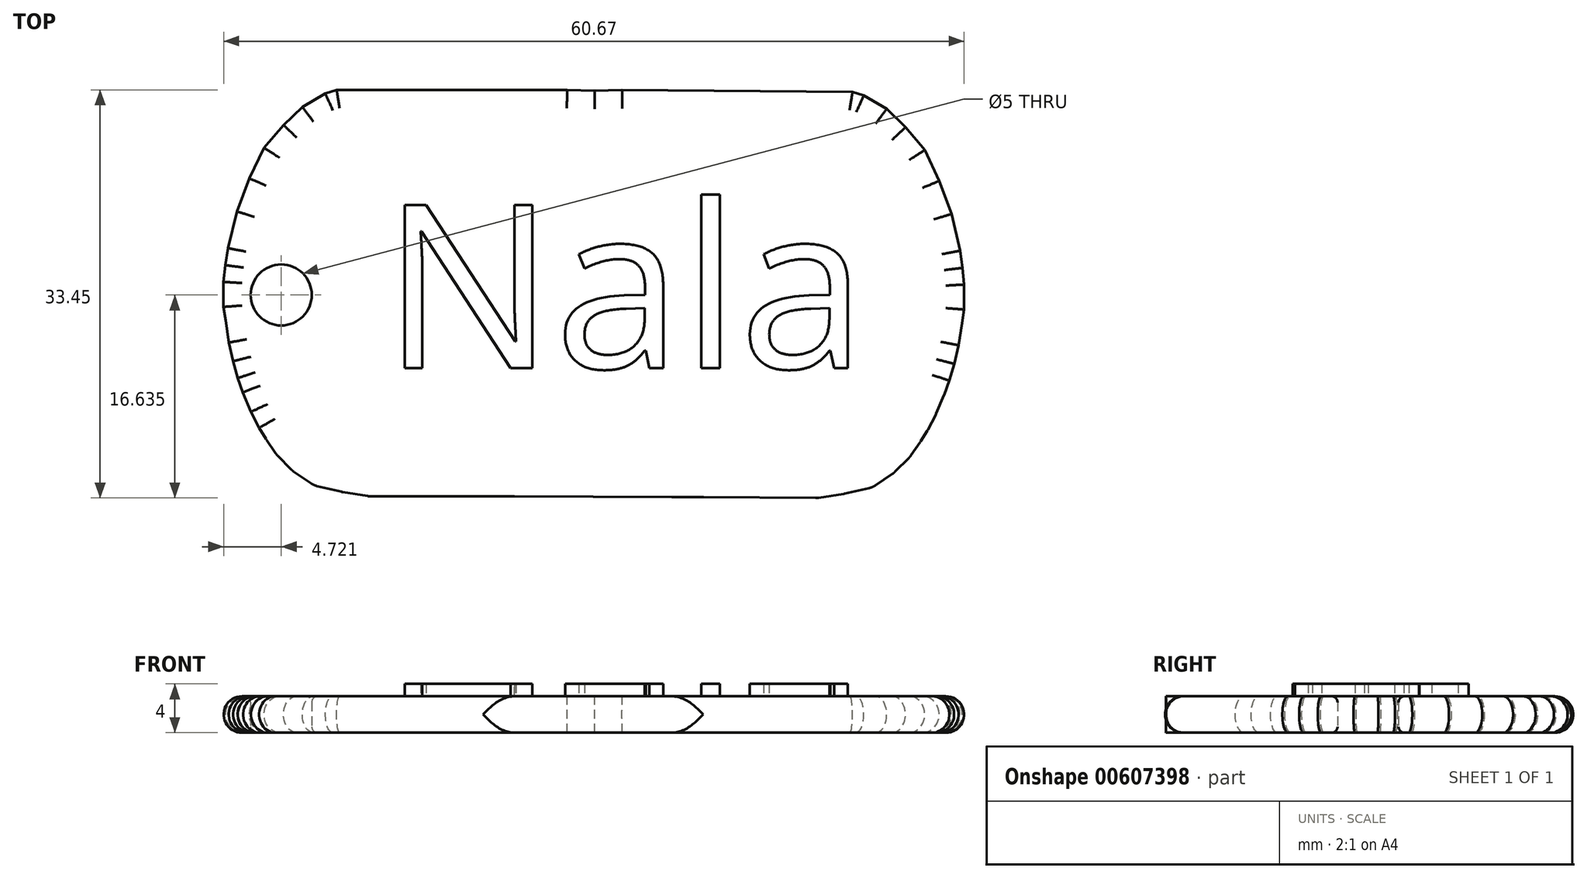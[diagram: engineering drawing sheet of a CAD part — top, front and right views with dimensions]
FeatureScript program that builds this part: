
annotation { "Feature Type Name" : "Feature", "Feature Type Description" : "" }
export const myFeature = defineFeature(function(context is Context, id is Id, definition is map)
    precondition{}
    {
        {
            var Q0;
            Q0=qCreatedBy(makeId("Top.planeOp"),FACE);
            var sketch = newSketch(context, id + "F0", { "sketchPlane" : qUnion([Q0])});
            skLineSegment(sketch, "E0", {"start": v(-37.9, 10.65) * mm, "end": v(-39.11, 8.12) * mm});
            skLineSegment(sketch, "E1", {"start": v(-39.11, 8.12) * mm, "end": v(-40.13, 5.41) * mm});
            skLineSegment(sketch, "E2", {"start": v(-40.13, 5.41) * mm, "end": v(-40.85, 2.4) * mm});
            skLineSegment(sketch, "E3", {"start": v(-40.85, 2.4) * mm, "end": v(-41.06, 1) * mm});
            skLineSegment(sketch, "E4", {"start": v(-41.06, 1) * mm, "end": v(-41.21, -0.37) * mm});
            skLineSegment(sketch, "E5", {"start": v(-41.21, -0.37) * mm, "end": v(-41.21, -2.41) * mm});
            skLineSegment(sketch, "E6", {"start": v(-41.21, -2.41) * mm, "end": v(-41.05, -3.53) * mm});
            skLineSegment(sketch, "E7", {"start": v(-41.05, -3.53) * mm, "end": v(-40.8, -5.34) * mm});
            skLineSegment(sketch, "E8", {"start": v(-40.8, -5.34) * mm, "end": v(-40.44, -6.87) * mm});
            skLineSegment(sketch, "E9", {"start": v(-40.44, -6.87) * mm, "end": v(-40.07, -8.25) * mm});
            skLineSegment(sketch, "E10", {"start": v(-40.07, -8.25) * mm, "end": v(-39.63, -9.42) * mm});
            skLineSegment(sketch, "E11", {"start": v(-39.63, -9.42) * mm, "end": v(-38.98, -11.01) * mm});
            skLineSegment(sketch, "E12", {"start": v(-38.98, -11.01) * mm, "end": v(-38.3, -12.33) * mm});
            skLineSegment(sketch, "E13", {"start": v(-38.3, -12.33) * mm, "end": v(-37.72, -13.27) * mm});
            skLineSegment(sketch, "E14", {"start": v(-37.72, -13.27) * mm, "end": v(-36.88, -14.5) * mm});
            skLineSegment(sketch, "E15", {"start": v(-36.88, -14.5) * mm, "end": v(-35.56, -15.85) * mm});
            skLineSegment(sketch, "E16", {"start": v(-35.56, -15.85) * mm, "end": v(-33.8, -17.04) * mm});
            skLineSegment(sketch, "E17", {"start": v(-33.8, -17.04) * mm, "end": v(-31.5, -17.58) * mm});
            skLineSegment(sketch, "E18", {"start": v(-31.5, -17.58) * mm, "end": v(-29.29, -17.94) * mm});
            skLineSegment(sketch, "E19", {"start": v(-29.29, -17.94) * mm, "end": v(-19.97, -17.94) * mm});
            skLineSegment(sketch, "E20", {"start": v(-37.9, 10.65) * mm, "end": v(-36.3, 12.49) * mm});
            skLineSegment(sketch, "E21", {"start": v(-36.3, 12.49) * mm, "end": v(-34.77, 13.98) * mm});
            skLineSegment(sketch, "E22", {"start": v(-34.77, 13.98) * mm, "end": v(-32.87, 15.08) * mm});
            skLineSegment(sketch, "E23", {"start": v(-32.87, 15.08) * mm, "end": v(-31.95, 15.38) * mm});
            skLineSegment(sketch, "E24", {"start": v(-31.95, 15.38) * mm, "end": v(-30.53, 15.38) * mm});
            skLineSegment(sketch, "E25", {"start": v(-30.53, 15.38) * mm, "end": v(-28.67, 15.38) * mm});
            skLineSegment(sketch, "E26", {"start": v(-28.67, 15.38) * mm, "end": v(-26.55, 15.38) * mm});
            skLineSegment(sketch, "E27", {"start": v(-26.55, 15.38) * mm, "end": v(-23.52, 15.38) * mm});
            skLineSegment(sketch, "E28", {"start": v(-23.52, 15.38) * mm, "end": v(-18.18, 15.38) * mm});
            skLineSegment(sketch, "E29", {"start": v(-18.18, 15.38) * mm, "end": v(-13.07, 15.38) * mm});
            skLineSegment(sketch, "E30", {"start": v(-13.07, 15.38) * mm, "end": v(-10.82, 15.3) * mm});
            skLineSegment(sketch, "E31", {"start": v(-10.82, 15.3) * mm, "end": v(-10.94, -17.58) * mm});
            skLineSegment(sketch, "E32.MirrorCS", {"start": v(-8.57, 15.36) * mm, "end": v(-10.82, 15.3) * mm});
            skLineSegment(sketch, "E33.MirrorCS", {"start": v(-3.46, 15.32) * mm, "end": v(-8.57, 15.36) * mm});
            skLineSegment(sketch, "E34.MirrorCS", {"start": v(1.88, 15.28) * mm, "end": v(-3.46, 15.32) * mm});
            skLineSegment(sketch, "E35.MirrorCS", {"start": v(4.91, 15.26) * mm, "end": v(1.88, 15.28) * mm});
            skLineSegment(sketch, "E36.MirrorCS", {"start": v(7.03, 15.25) * mm, "end": v(4.91, 15.26) * mm});
            skLineSegment(sketch, "E37.MirrorCS", {"start": v(8.9, 15.23) * mm, "end": v(7.03, 15.25) * mm});
            skLineSegment(sketch, "E38.MirrorCS", {"start": v(10.31, 15.22) * mm, "end": v(8.9, 15.23) * mm});
            skLineSegment(sketch, "E39.MirrorCS", {"start": v(11.23, 14.92) * mm, "end": v(10.31, 15.22) * mm});
            skLineSegment(sketch, "E40.MirrorCS", {"start": v(13.12, 13.8) * mm, "end": v(11.23, 14.92) * mm});
            skLineSegment(sketch, "E41.MirrorCS", {"start": v(14.65, 12.3) * mm, "end": v(13.12, 13.8) * mm});
            skLineSegment(sketch, "E42.MirrorCS", {"start": v(16.23, 10.45) * mm, "end": v(14.65, 12.3) * mm});
            skLineSegment(sketch, "E43.MirrorCS", {"start": v(16.23, 10.45) * mm, "end": v(17.42, 7.91) * mm});
            skLineSegment(sketch, "E44.MirrorCS", {"start": v(17.42, 7.91) * mm, "end": v(18.42, 5.2) * mm});
            skLineSegment(sketch, "E45.MirrorCS", {"start": v(18.42, 5.2) * mm, "end": v(19.12, 2.19) * mm});
            skLineSegment(sketch, "E46.MirrorCS", {"start": v(19.12, 2.19) * mm, "end": v(19.31, 0.79) * mm});
            skLineSegment(sketch, "E47.MirrorCS", {"start": v(19.31, 0.79) * mm, "end": v(19.46, -0.59) * mm});
            skLineSegment(sketch, "E48.MirrorCS", {"start": v(19.46, -0.59) * mm, "end": v(19.45, -2.63) * mm});
            skLineSegment(sketch, "E49.MirrorCS", {"start": v(19.45, -2.63) * mm, "end": v(19.27, -3.74) * mm});
            skLineSegment(sketch, "E50.MirrorCS", {"start": v(19.27, -3.74) * mm, "end": v(19, -5.55) * mm});
            skLineSegment(sketch, "E51.MirrorCS", {"start": v(19, -5.55) * mm, "end": v(18.64, -7.08) * mm});
            skLineSegment(sketch, "E52.MirrorCS", {"start": v(18.64, -7.08) * mm, "end": v(18.25, -8.46) * mm});
            skLineSegment(sketch, "E53.MirrorCS", {"start": v(18.25, -8.46) * mm, "end": v(17.8, -9.63) * mm});
            skLineSegment(sketch, "E54.MirrorCS", {"start": v(17.8, -9.63) * mm, "end": v(17.15, -11.21) * mm});
            skLineSegment(sketch, "E55.MirrorCS", {"start": v(17.15, -11.21) * mm, "end": v(16.47, -12.53) * mm});
            skLineSegment(sketch, "E56.MirrorCS", {"start": v(16.47, -12.53) * mm, "end": v(15.87, -13.46) * mm});
            skLineSegment(sketch, "E57.MirrorCS", {"start": v(15.87, -13.46) * mm, "end": v(15.03, -14.7) * mm});
            skLineSegment(sketch, "E58.MirrorCS", {"start": v(15.03, -14.7) * mm, "end": v(13.7, -16.02) * mm});
            skLineSegment(sketch, "E59.MirrorCS", {"start": v(13.7, -16.02) * mm, "end": v(11.93, -17.2) * mm});
            skLineSegment(sketch, "E60.MirrorCS", {"start": v(11.93, -17.2) * mm, "end": v(9.63, -17.73) * mm});
            skLineSegment(sketch, "E61.MirrorCS", {"start": v(9.63, -17.73) * mm, "end": v(7.4, -18.07) * mm});
            skLineSegment(sketch, "E62.MirrorCS", {"start": v(7.4, -18.07) * mm, "end": v(-1.9, -18) * mm});
            skCircle(sketch, "E63", {"center": v(-36.49, -1.43) * mm, "radius": 2.5 * mm});
            skLineSegment(sketch, "E64", {"start": v(-19.97, -17.94) * mm, "end": v(-1.9, -18) * mm});
            skSolve(sketch);
        }
        {
            var Q0;
            Q0 = qSketchRegion(id + "F0", true);
            var Q1;
            Q1=makeQuery(id+"F0.imprint","IMPRINT",FACE,{"disambiguationData":[TD([[makeQuery(id+"F0.imprint","IMPRINT",EDGE,{"derivedFrom":sQuery(id+"F0.wireOp",EDGE,"E0")}),1.0]])]});
            extrude(context, id + "F1", {"entities" : qUnion([Q0, Q1]), "depth" : 3 * mm, "offsetDistance" : 25 * mm});
        }
        {
            var Q0;
            Q0=makeQuery(id+"F1.opExtrude","CAP_EDGE",EDGE,{"disambiguationData":[OSD([sQuery(id+"F0.wireOp",EDGE,"E19")])],"isStart":false});
            var Q1;
            Q1=makeQuery(id+"F1.opExtrude","CAP_EDGE",EDGE,{"disambiguationData":[OSD([sQuery(id+"F0.wireOp",EDGE,"WqU1F3oS-ofhP-bZeb-JVwl-enVTnePdHite")])],"isStart":false});
            var Q2;
            Q2=makeQuery(id+"F1.opExtrude","CAP_EDGE",EDGE,{"disambiguationData":[OSD([sQuery(id+"F0.wireOp",EDGE,"QgttkmmI-ZrSr-rnyg-uRgk-pYvE0oLxrQIC"),sQuery(id+"F0.wireOp",EDGE,"cICnWOkE-zCsr-WVfL-8WAR-oVfGwmKeuLjA")])],"isStart":false});
            var Q3;
            Q3=makeQuery(id+"F1.opExtrude","CAP_EDGE",EDGE,{"disambiguationData":[OSD([sQuery(id+"F0.wireOp",EDGE,"5ab367f4-9cd3-4356-90f0-5b2019c22e200.MirrorCS"),sQuery(id+"F0.wireOp",EDGE,"096961d2-05df-4f17-8771-bd5e1e9e85af0.MirrorCS")])],"isStart":false});
            var Q4;
            Q4=makeQuery(id+"F1.opExtrude","CAP_EDGE",EDGE,{"disambiguationData":[OSD([sQuery(id+"F0.wireOp",EDGE,"e1c94456-ab08-4bec-9781-fa68d74f9dfd0.MirrorCS")])],"isStart":false});
            var Q5;
            Q5=makeQuery(id+"F1.opExtrude","CAP_EDGE",EDGE,{"disambiguationData":[OSD([sQuery(id+"F0.wireOp",EDGE,"E62.MirrorCS")])],"isStart":false});
            var Q6;
            Q6=makeQuery(id+"F1.opExtrude","CAP_EDGE",EDGE,{"disambiguationData":[OSD([sQuery(id+"F0.wireOp",EDGE,"E60.MirrorCS")])],"isStart":false});
            var Q7;
            Q7=makeQuery(id+"F1.opExtrude","CAP_EDGE",EDGE,{"disambiguationData":[OSD([sQuery(id+"F0.wireOp",EDGE,"E61.MirrorCS")])],"isStart":false});
            var Q8;
            Q8=makeQuery(id+"F1.opExtrude","CAP_EDGE",EDGE,{"disambiguationData":[OSD([sQuery(id+"F0.wireOp",EDGE,"E59.MirrorCS")])],"isStart":false});
            var Q9;
            Q9=makeQuery(id+"F1.opExtrude","CAP_EDGE",EDGE,{"disambiguationData":[OSD([sQuery(id+"F0.wireOp",EDGE,"E58.MirrorCS")])],"isStart":false});
            var Q10;
            Q10=makeQuery(id+"F1.opExtrude","CAP_EDGE",EDGE,{"disambiguationData":[OSD([sQuery(id+"F0.wireOp",EDGE,"E56.MirrorCS")])],"isStart":false});
            var Q11;
            Q11=makeQuery(id+"F1.opExtrude","CAP_EDGE",EDGE,{"disambiguationData":[OSD([sQuery(id+"F0.wireOp",EDGE,"E57.MirrorCS")])],"isStart":false});
            var Q12;
            Q12=makeQuery(id+"F1.opExtrude","CAP_EDGE",EDGE,{"disambiguationData":[OSD([sQuery(id+"F0.wireOp",EDGE,"E55.MirrorCS")])],"isStart":false});
            var Q13;
            Q13=makeQuery(id+"F1.opExtrude","CAP_EDGE",EDGE,{"disambiguationData":[OSD([sQuery(id+"F0.wireOp",EDGE,"E54.MirrorCS")])],"isStart":false});
            var Q14;
            Q14=makeQuery(id+"F1.opExtrude","CAP_EDGE",EDGE,{"disambiguationData":[OSD([sQuery(id+"F0.wireOp",EDGE,"E53.MirrorCS")])],"isStart":false});
            var Q15;
            Q15=makeQuery(id+"F1.opExtrude","CAP_EDGE",EDGE,{"disambiguationData":[OSD([sQuery(id+"F0.wireOp",EDGE,"E52.MirrorCS")])],"isStart":false});
            var Q16;
            Q16=makeQuery(id+"F1.opExtrude","CAP_EDGE",EDGE,{"disambiguationData":[OSD([sQuery(id+"F0.wireOp",EDGE,"E51.MirrorCS")])],"isStart":false});
            var Q17;
            Q17=makeQuery(id+"F1.opExtrude","CAP_EDGE",EDGE,{"disambiguationData":[OSD([sQuery(id+"F0.wireOp",EDGE,"E50.MirrorCS")])],"isStart":false});
            var Q18;
            Q18=makeQuery(id+"F1.opExtrude","CAP_EDGE",EDGE,{"disambiguationData":[OSD([sQuery(id+"F0.wireOp",EDGE,"E49.MirrorCS")])],"isStart":false});
            var Q19;
            Q19=makeQuery(id+"F1.opExtrude","CAP_EDGE",EDGE,{"disambiguationData":[OSD([sQuery(id+"F0.wireOp",EDGE,"E48.MirrorCS")])],"isStart":false});
            var Q20;
            Q20=makeQuery(id+"F1.opExtrude","CAP_EDGE",EDGE,{"disambiguationData":[OSD([sQuery(id+"F0.wireOp",EDGE,"E47.MirrorCS")])],"isStart":false});
            var Q21;
            Q21=makeQuery(id+"F1.opExtrude","CAP_EDGE",EDGE,{"disambiguationData":[OSD([sQuery(id+"F0.wireOp",EDGE,"E46.MirrorCS")])],"isStart":false});
            var Q22;
            Q22=makeQuery(id+"F1.opExtrude","CAP_EDGE",EDGE,{"disambiguationData":[OSD([sQuery(id+"F0.wireOp",EDGE,"E45.MirrorCS")])],"isStart":false});
            var Q23;
            Q23=makeQuery(id+"F1.opExtrude","CAP_EDGE",EDGE,{"disambiguationData":[OSD([sQuery(id+"F0.wireOp",EDGE,"E44.MirrorCS")])],"isStart":false});
            var Q24;
            Q24=makeQuery(id+"F1.opExtrude","CAP_EDGE",EDGE,{"disambiguationData":[OSD([sQuery(id+"F0.wireOp",EDGE,"E43.MirrorCS")])],"isStart":false});
            var Q25;
            Q25=makeQuery(id+"F1.opExtrude","CAP_EDGE",EDGE,{"disambiguationData":[OSD([sQuery(id+"F0.wireOp",EDGE,"E42.MirrorCS")])],"isStart":false});
            var Q26;
            Q26=makeQuery(id+"F1.opExtrude","CAP_EDGE",EDGE,{"disambiguationData":[OSD([sQuery(id+"F0.wireOp",EDGE,"E41.MirrorCS")])],"isStart":false});
            var Q27;
            Q27=makeQuery(id+"F1.opExtrude","CAP_EDGE",EDGE,{"disambiguationData":[OSD([sQuery(id+"F0.wireOp",EDGE,"E40.MirrorCS")])],"isStart":false});
            var Q28;
            Q28=makeQuery(id+"F1.opExtrude","CAP_EDGE",EDGE,{"disambiguationData":[OSD([sQuery(id+"F0.wireOp",EDGE,"E33.MirrorCS"),sQuery(id+"F0.wireOp",EDGE,"E34.MirrorCS"),sQuery(id+"F0.wireOp",EDGE,"E35.MirrorCS"),sQuery(id+"F0.wireOp",EDGE,"E36.MirrorCS"),sQuery(id+"F0.wireOp",EDGE,"E37.MirrorCS"),sQuery(id+"F0.wireOp",EDGE,"E38.MirrorCS")])],"isStart":false});
            var Q29;
            Q29=makeQuery(id+"F1.opExtrude","CAP_EDGE",EDGE,{"disambiguationData":[OSD([sQuery(id+"F0.wireOp",EDGE,"E39.MirrorCS")])],"isStart":false});
            var Q30;
            Q30=makeQuery(id+"F1.opExtrude","CAP_EDGE",EDGE,{"disambiguationData":[OSD([sQuery(id+"F0.wireOp",EDGE,"E32.MirrorCS")])],"isStart":false});
            var Q31;
            Q31=makeQuery(id+"F1.opExtrude","CAP_EDGE",EDGE,{"disambiguationData":[OSD([sQuery(id+"F0.wireOp",EDGE,"E30")])],"isStart":false});
            var Q32;
            Q32=makeQuery(id+"F1.opExtrude","CAP_EDGE",EDGE,{"disambiguationData":[OSD([sQuery(id+"F0.wireOp",EDGE,"E24"),sQuery(id+"F0.wireOp",EDGE,"E25"),sQuery(id+"F0.wireOp",EDGE,"E26"),sQuery(id+"F0.wireOp",EDGE,"E27"),sQuery(id+"F0.wireOp",EDGE,"E28"),sQuery(id+"F0.wireOp",EDGE,"E29")])],"isStart":false});
            var Q33;
            Q33=makeQuery(id+"F1.opExtrude","CAP_EDGE",EDGE,{"disambiguationData":[OSD([sQuery(id+"F0.wireOp",EDGE,"E23")])],"isStart":false});
            var Q34;
            Q34=makeQuery(id+"F1.opExtrude","CAP_EDGE",EDGE,{"disambiguationData":[OSD([sQuery(id+"F0.wireOp",EDGE,"E22")])],"isStart":false});
            var Q35;
            Q35=makeQuery(id+"F1.opExtrude","CAP_EDGE",EDGE,{"disambiguationData":[OSD([sQuery(id+"F0.wireOp",EDGE,"E20")])],"isStart":false});
            var Q36;
            Q36=makeQuery(id+"F1.opExtrude","CAP_EDGE",EDGE,{"disambiguationData":[OSD([sQuery(id+"F0.wireOp",EDGE,"E21")])],"isStart":false});
            var Q37;
            Q37=makeQuery(id+"F1.opExtrude","CAP_EDGE",EDGE,{"disambiguationData":[OSD([sQuery(id+"F0.wireOp",EDGE,"E0")])],"isStart":false});
            var Q38;
            Q38=makeQuery(id+"F1.opExtrude","CAP_EDGE",EDGE,{"disambiguationData":[OSD([sQuery(id+"F0.wireOp",EDGE,"E1")])],"isStart":false});
            var Q39;
            Q39=makeQuery(id+"F1.opExtrude","CAP_EDGE",EDGE,{"disambiguationData":[OSD([sQuery(id+"F0.wireOp",EDGE,"E2")])],"isStart":false});
            var Q40;
            Q40=makeQuery(id+"F1.opExtrude","CAP_EDGE",EDGE,{"disambiguationData":[OSD([sQuery(id+"F0.wireOp",EDGE,"E3")])],"isStart":false});
            var Q41;
            Q41=makeQuery(id+"F1.opExtrude","CAP_EDGE",EDGE,{"disambiguationData":[OSD([sQuery(id+"F0.wireOp",EDGE,"E4")])],"isStart":false});
            var Q42;
            Q42=makeQuery(id+"F1.opExtrude","CAP_EDGE",EDGE,{"disambiguationData":[OSD([sQuery(id+"F0.wireOp",EDGE,"E5")])],"isStart":false});
            var Q43;
            Q43=makeQuery(id+"F1.opExtrude","CAP_EDGE",EDGE,{"disambiguationData":[OSD([sQuery(id+"F0.wireOp",EDGE,"E6")])],"isStart":false});
            var Q44;
            Q44=makeQuery(id+"F1.opExtrude","CAP_EDGE",EDGE,{"disambiguationData":[OSD([sQuery(id+"F0.wireOp",EDGE,"E7")])],"isStart":false});
            var Q45;
            Q45=makeQuery(id+"F1.opExtrude","CAP_EDGE",EDGE,{"disambiguationData":[OSD([sQuery(id+"F0.wireOp",EDGE,"E8")])],"isStart":false});
            var Q46;
            Q46=makeQuery(id+"F1.opExtrude","CAP_EDGE",EDGE,{"disambiguationData":[OSD([sQuery(id+"F0.wireOp",EDGE,"E9")])],"isStart":false});
            var Q47;
            Q47=makeQuery(id+"F1.opExtrude","CAP_EDGE",EDGE,{"disambiguationData":[OSD([sQuery(id+"F0.wireOp",EDGE,"E10")])],"isStart":false});
            var Q48;
            Q48=makeQuery(id+"F1.opExtrude","CAP_EDGE",EDGE,{"disambiguationData":[OSD([sQuery(id+"F0.wireOp",EDGE,"E11")])],"isStart":false});
            var Q49;
            Q49=makeQuery(id+"F1.opExtrude","CAP_EDGE",EDGE,{"disambiguationData":[OSD([sQuery(id+"F0.wireOp",EDGE,"E12")])],"isStart":false});
            var Q50;
            Q50=makeQuery(id+"F1.opExtrude","CAP_EDGE",EDGE,{"disambiguationData":[OSD([sQuery(id+"F0.wireOp",EDGE,"E13")])],"isStart":false});
            var Q51;
            Q51=makeQuery(id+"F1.opExtrude","CAP_EDGE",EDGE,{"disambiguationData":[OSD([sQuery(id+"F0.wireOp",EDGE,"E14")])],"isStart":false});
            var Q52;
            Q52=makeQuery(id+"F1.opExtrude","CAP_EDGE",EDGE,{"disambiguationData":[OSD([sQuery(id+"F0.wireOp",EDGE,"E15")])],"isStart":false});
            var Q53;
            Q53=makeQuery(id+"F1.opExtrude","CAP_EDGE",EDGE,{"disambiguationData":[OSD([sQuery(id+"F0.wireOp",EDGE,"E17")])],"isStart":false});
            var Q54;
            Q54=makeQuery(id+"F1.opExtrude","CAP_EDGE",EDGE,{"disambiguationData":[OSD([sQuery(id+"F0.wireOp",EDGE,"E16")])],"isStart":false});
            var Q55;
            Q55=makeQuery(id+"F1.opExtrude","CAP_EDGE",EDGE,{"disambiguationData":[OSD([sQuery(id+"F0.wireOp",EDGE,"E18")])],"isStart":false});
            var Q56;
            Q56=makeQuery(id+"F1.opExtrude","CAP_EDGE",EDGE,{"disambiguationData":[OSD([sQuery(id+"F0.wireOp",EDGE,"E3")])],"isStart":true});
            var Q57;
            Q57=makeQuery(id+"F1.opExtrude","CAP_EDGE",EDGE,{"disambiguationData":[OSD([sQuery(id+"F0.wireOp",EDGE,"E4")])],"isStart":true});
            var Q58;
            Q58=makeQuery(id+"F1.opExtrude","CAP_EDGE",EDGE,{"disambiguationData":[OSD([sQuery(id+"F0.wireOp",EDGE,"E5")])],"isStart":true});
            var Q59;
            Q59=makeQuery(id+"F1.opExtrude","CAP_EDGE",EDGE,{"disambiguationData":[OSD([sQuery(id+"F0.wireOp",EDGE,"E6")])],"isStart":true});
            var Q60;
            Q60=makeQuery(id+"F1.opExtrude","CAP_EDGE",EDGE,{"disambiguationData":[OSD([sQuery(id+"F0.wireOp",EDGE,"E8")])],"isStart":true});
            var Q61;
            Q61=makeQuery(id+"F1.opExtrude","CAP_EDGE",EDGE,{"disambiguationData":[OSD([sQuery(id+"F0.wireOp",EDGE,"E9")])],"isStart":true});
            var Q62;
            Q62=makeQuery(id+"F1.opExtrude","CAP_EDGE",EDGE,{"disambiguationData":[OSD([sQuery(id+"F0.wireOp",EDGE,"E10")])],"isStart":true});
            var Q63;
            Q63=makeQuery(id+"F1.opExtrude","CAP_EDGE",EDGE,{"disambiguationData":[OSD([sQuery(id+"F0.wireOp",EDGE,"E11")])],"isStart":true});
            var Q64;
            Q64=makeQuery(id+"F1.opExtrude","CAP_EDGE",EDGE,{"disambiguationData":[OSD([sQuery(id+"F0.wireOp",EDGE,"E12")])],"isStart":true});
            var Q65;
            Q65=makeQuery(id+"F1.opExtrude","CAP_EDGE",EDGE,{"disambiguationData":[OSD([sQuery(id+"F0.wireOp",EDGE,"E7")])],"isStart":true});
            var Q66;
            Q66=makeQuery(id+"F1.opExtrude","CAP_EDGE",EDGE,{"disambiguationData":[OSD([sQuery(id+"F0.wireOp",EDGE,"E2")])],"isStart":true});
            var Q67;
            Q67=makeQuery(id+"F1.opExtrude","CAP_EDGE",EDGE,{"disambiguationData":[OSD([sQuery(id+"F0.wireOp",EDGE,"E0")])],"isStart":true});
            var Q68;
            Q68=makeQuery(id+"F1.opExtrude","CAP_EDGE",EDGE,{"disambiguationData":[OSD([sQuery(id+"F0.wireOp",EDGE,"E1")])],"isStart":true});
            var Q69;
            Q69=makeQuery(id+"F1.opExtrude","CAP_EDGE",EDGE,{"disambiguationData":[OSD([sQuery(id+"F0.wireOp",EDGE,"E20")])],"isStart":true});
            var Q70;
            Q70=makeQuery(id+"F1.opExtrude","CAP_EDGE",EDGE,{"disambiguationData":[OSD([sQuery(id+"F0.wireOp",EDGE,"E21")])],"isStart":true});
            var Q71;
            Q71=makeQuery(id+"F1.opExtrude","CAP_EDGE",EDGE,{"disambiguationData":[OSD([sQuery(id+"F0.wireOp",EDGE,"E22")])],"isStart":true});
            var Q72;
            Q72=makeQuery(id+"F1.opExtrude","CAP_EDGE",EDGE,{"disambiguationData":[OSD([sQuery(id+"F0.wireOp",EDGE,"E23")])],"isStart":true});
            var Q73;
            Q73=makeQuery(id+"F1.opExtrude","CAP_EDGE",EDGE,{"disambiguationData":[OSD([sQuery(id+"F0.wireOp",EDGE,"E24"),sQuery(id+"F0.wireOp",EDGE,"E25"),sQuery(id+"F0.wireOp",EDGE,"E26"),sQuery(id+"F0.wireOp",EDGE,"E27"),sQuery(id+"F0.wireOp",EDGE,"E28"),sQuery(id+"F0.wireOp",EDGE,"E29")])],"isStart":true});
            var Q74;
            Q74=makeQuery(id+"F1.opExtrude","CAP_EDGE",EDGE,{"disambiguationData":[OSD([sQuery(id+"F0.wireOp",EDGE,"E30")])],"isStart":true});
            var Q75;
            Q75=makeQuery(id+"F1.opExtrude","CAP_EDGE",EDGE,{"disambiguationData":[OSD([sQuery(id+"F0.wireOp",EDGE,"E32.MirrorCS")])],"isStart":true});
            var Q76;
            Q76=makeQuery(id+"F1.opExtrude","CAP_EDGE",EDGE,{"disambiguationData":[OSD([sQuery(id+"F0.wireOp",EDGE,"E33.MirrorCS"),sQuery(id+"F0.wireOp",EDGE,"E34.MirrorCS"),sQuery(id+"F0.wireOp",EDGE,"E35.MirrorCS"),sQuery(id+"F0.wireOp",EDGE,"E36.MirrorCS"),sQuery(id+"F0.wireOp",EDGE,"E37.MirrorCS"),sQuery(id+"F0.wireOp",EDGE,"E38.MirrorCS")])],"isStart":true});
            var Q77;
            Q77=makeQuery(id+"F1.opExtrude","CAP_EDGE",EDGE,{"disambiguationData":[OSD([sQuery(id+"F0.wireOp",EDGE,"E39.MirrorCS")])],"isStart":true});
            var Q78;
            Q78=makeQuery(id+"F1.opExtrude","CAP_EDGE",EDGE,{"disambiguationData":[OSD([sQuery(id+"F0.wireOp",EDGE,"E40.MirrorCS")])],"isStart":true});
            var Q79;
            Q79=makeQuery(id+"F1.opExtrude","CAP_EDGE",EDGE,{"disambiguationData":[OSD([sQuery(id+"F0.wireOp",EDGE,"E44.MirrorCS")])],"isStart":true});
            var Q80;
            Q80=makeQuery(id+"F1.opExtrude","CAP_EDGE",EDGE,{"disambiguationData":[OSD([sQuery(id+"F0.wireOp",EDGE,"E45.MirrorCS")])],"isStart":true});
            var Q81;
            Q81=makeQuery(id+"F1.opExtrude","CAP_EDGE",EDGE,{"disambiguationData":[OSD([sQuery(id+"F0.wireOp",EDGE,"E43.MirrorCS")])],"isStart":true});
            var Q82;
            Q82=makeQuery(id+"F1.opExtrude","CAP_EDGE",EDGE,{"disambiguationData":[OSD([sQuery(id+"F0.wireOp",EDGE,"E42.MirrorCS")])],"isStart":true});
            var Q83;
            Q83=makeQuery(id+"F1.opExtrude","CAP_EDGE",EDGE,{"disambiguationData":[OSD([sQuery(id+"F0.wireOp",EDGE,"E41.MirrorCS")])],"isStart":true});
            var Q84;
            Q84=makeQuery(id+"F1.opExtrude","CAP_EDGE",EDGE,{"disambiguationData":[OSD([sQuery(id+"F0.wireOp",EDGE,"E46.MirrorCS")])],"isStart":true});
            var Q85;
            Q85=makeQuery(id+"F1.opExtrude","CAP_EDGE",EDGE,{"disambiguationData":[OSD([sQuery(id+"F0.wireOp",EDGE,"E47.MirrorCS")])],"isStart":true});
            var Q86;
            Q86=makeQuery(id+"F1.opExtrude","CAP_EDGE",EDGE,{"disambiguationData":[OSD([sQuery(id+"F0.wireOp",EDGE,"E48.MirrorCS")])],"isStart":true});
            var Q87;
            Q87=makeQuery(id+"F1.opExtrude","CAP_EDGE",EDGE,{"disambiguationData":[OSD([sQuery(id+"F0.wireOp",EDGE,"E49.MirrorCS")])],"isStart":true});
            var Q88;
            Q88=makeQuery(id+"F1.opExtrude","CAP_EDGE",EDGE,{"disambiguationData":[OSD([sQuery(id+"F0.wireOp",EDGE,"E50.MirrorCS")])],"isStart":true});
            var Q89;
            Q89=makeQuery(id+"F1.opExtrude","CAP_EDGE",EDGE,{"disambiguationData":[OSD([sQuery(id+"F0.wireOp",EDGE,"E51.MirrorCS")])],"isStart":true});
            var Q90;
            Q90=makeQuery(id+"F1.opExtrude","CAP_EDGE",EDGE,{"disambiguationData":[OSD([sQuery(id+"F0.wireOp",EDGE,"E52.MirrorCS")])],"isStart":true});
            var Q91;
            Q91=makeQuery(id+"F1.opExtrude","CAP_EDGE",EDGE,{"disambiguationData":[OSD([sQuery(id+"F0.wireOp",EDGE,"E55.MirrorCS")])],"isStart":true});
            var Q92;
            Q92=makeQuery(id+"F1.opExtrude","CAP_EDGE",EDGE,{"disambiguationData":[OSD([sQuery(id+"F0.wireOp",EDGE,"E59.MirrorCS")])],"isStart":true});
            var Q93;
            Q93=makeQuery(id+"F1.opExtrude","CAP_EDGE",EDGE,{"disambiguationData":[OSD([sQuery(id+"F0.wireOp",EDGE,"E16")])],"isStart":true});
            var Q94;
            Q94=makeQuery(id+"F1.opExtrude","CAP_EDGE",EDGE,{"disambiguationData":[OSD([sQuery(id+"F0.wireOp",EDGE,"E15")])],"isStart":true});
            var Q95;
            Q95=makeQuery(id+"F1.opExtrude","CAP_EDGE",EDGE,{"disambiguationData":[OSD([sQuery(id+"F0.wireOp",EDGE,"E56.MirrorCS")])],"isStart":true});
            var Q96;
            Q96=makeQuery(id+"F1.opExtrude","CAP_EDGE",EDGE,{"disambiguationData":[OSD([sQuery(id+"F0.wireOp",EDGE,"E17")])],"isStart":true});
            var Q97;
            Q97=makeQuery(id+"F1.opExtrude","CAP_EDGE",EDGE,{"disambiguationData":[OSD([sQuery(id+"F0.wireOp",EDGE,"E62.MirrorCS")])],"isStart":true});
            var Q98;
            Q98=makeQuery(id+"F1.opExtrude","SWEPT_EDGE",EDGE,{"disambiguationData":[OSD([sQuery(id+"F0.wireOp",EDGE,"E58.MirrorCS"),sQuery(id+"F0.wireOp",EDGE,"E59.MirrorCS")])]});
            var Q99;
            Q99=makeQuery(id+"F1.opExtrude","SWEPT_EDGE",EDGE,{"disambiguationData":[OSD([sQuery(id+"F0.wireOp",EDGE,"E57.MirrorCS"),sQuery(id+"F0.wireOp",EDGE,"E58.MirrorCS")])]});
            var Q100;
            Q100=makeQuery(id+"F1.opExtrude","CAP_EDGE",EDGE,{"disambiguationData":[OSD([sQuery(id+"F0.wireOp",EDGE,"E54.MirrorCS")])],"isStart":true});
            var Q101;
            Q101=makeQuery(id+"F1.opExtrude","SWEPT_EDGE",EDGE,{"disambiguationData":[OSD([sQuery(id+"F0.wireOp",EDGE,"E56.MirrorCS"),sQuery(id+"F0.wireOp",EDGE,"E57.MirrorCS")])]});
            var Q102;
            Q102=makeQuery(id+"F1.opExtrude","SWEPT_EDGE",EDGE,{"disambiguationData":[OSD([sQuery(id+"F0.wireOp",EDGE,"E15"),sQuery(id+"F0.wireOp",EDGE,"E16")])]});
            var Q103;
            Q103=makeQuery(id+"F1.opExtrude","SWEPT_EDGE",EDGE,{"disambiguationData":[OSD([sQuery(id+"F0.wireOp",EDGE,"E55.MirrorCS"),sQuery(id+"F0.wireOp",EDGE,"E56.MirrorCS")])]});
            var Q104;
            Q104=makeQuery(id+"F1.opExtrude","CAP_EDGE",EDGE,{"disambiguationData":[OSD([sQuery(id+"F0.wireOp",EDGE,"e1c94456-ab08-4bec-9781-fa68d74f9dfd0.MirrorCS")])],"isStart":true});
            var Q105;
            Q105=makeQuery(id+"F1.opExtrude","CAP_EDGE",EDGE,{"disambiguationData":[OSD([sQuery(id+"F0.wireOp",EDGE,"QgttkmmI-ZrSr-rnyg-uRgk-pYvE0oLxrQIC"),sQuery(id+"F0.wireOp",EDGE,"cICnWOkE-zCsr-WVfL-8WAR-oVfGwmKeuLjA")])],"isStart":true});
            var Q106;
            Q106=makeQuery(id+"F1.opExtrude","SWEPT_EDGE",EDGE,{"disambiguationData":[OSD([sQuery(id+"F0.wireOp",EDGE,"E54.MirrorCS"),sQuery(id+"F0.wireOp",EDGE,"E53.MirrorCS")])]});
            var Q107;
            Q107=makeQuery(id+"F1.opExtrude","CAP_EDGE",EDGE,{"disambiguationData":[OSD([sQuery(id+"F0.wireOp",EDGE,"E61.MirrorCS")])],"isStart":true});
            var Q108;
            Q108=makeQuery(id+"F1.opExtrude","CAP_EDGE",EDGE,{"disambiguationData":[OSD([sQuery(id+"F0.wireOp",EDGE,"WqU1F3oS-ofhP-bZeb-JVwl-enVTnePdHite")])],"isStart":true});
            var Q109;
            Q109=makeQuery(id+"F1.opExtrude","CAP_EDGE",EDGE,{"disambiguationData":[OSD([sQuery(id+"F0.wireOp",EDGE,"E60.MirrorCS")])],"isStart":true});
            var Q110;
            Q110=makeQuery(id+"F1.opExtrude","CAP_EDGE",EDGE,{"disambiguationData":[OSD([sQuery(id+"F0.wireOp",EDGE,"E19")])],"isStart":true});
            var Q111;
            Q111=makeQuery(id+"F1.opExtrude","CAP_EDGE",EDGE,{"disambiguationData":[OSD([sQuery(id+"F0.wireOp",EDGE,"E57.MirrorCS")])],"isStart":true});
            var Q112;
            Q112=makeQuery(id+"F1.opExtrude","SWEPT_EDGE",EDGE,{"disambiguationData":[OSD([sQuery(id+"F0.wireOp",EDGE,"E13"),sQuery(id+"F0.wireOp",EDGE,"E14")])]});
            var Q113;
            Q113=makeQuery(id+"F1.opExtrude","SWEPT_EDGE",EDGE,{"disambiguationData":[OSD([sQuery(id+"F0.wireOp",EDGE,"E14"),sQuery(id+"F0.wireOp",EDGE,"E15")])]});
            var Q114;
            Q114=makeQuery(id+"F1.opExtrude","SWEPT_EDGE",EDGE,{"disambiguationData":[OSD([sQuery(id+"F0.wireOp",EDGE,"E61.MirrorCS"),sQuery(id+"F0.wireOp",EDGE,"E62.MirrorCS")])]});
            var Q115;
            Q115=makeQuery(id+"F1.opExtrude","SWEPT_EDGE",EDGE,{"disambiguationData":[OSD([sQuery(id+"F0.wireOp",EDGE,"E59.MirrorCS"),sQuery(id+"F0.wireOp",EDGE,"E60.MirrorCS")])]});
            var Q116;
            Q116=makeQuery(id+"F1.opExtrude","SWEPT_EDGE",EDGE,{"disambiguationData":[OSD([sQuery(id+"F0.wireOp",EDGE,"WqU1F3oS-ofhP-bZeb-JVwl-enVTnePdHite"),sQuery(id+"F0.wireOp",EDGE,"QgttkmmI-ZrSr-rnyg-uRgk-pYvE0oLxrQIC")])]});
            var Q117;
            Q117=makeQuery(id+"F1.opExtrude","CAP_EDGE",EDGE,{"disambiguationData":[OSD([sQuery(id+"F0.wireOp",EDGE,"E13")])],"isStart":true});
            var Q118;
            Q118=makeQuery(id+"F1.opExtrude","CAP_EDGE",EDGE,{"disambiguationData":[OSD([sQuery(id+"F0.wireOp",EDGE,"E18")])],"isStart":true});
            var Q119;
            Q119=makeQuery(id+"F1.opExtrude","SWEPT_EDGE",EDGE,{"disambiguationData":[OSD([sQuery(id+"F0.wireOp",EDGE,"E19"),sQuery(id+"F0.wireOp",EDGE,"WqU1F3oS-ofhP-bZeb-JVwl-enVTnePdHite")])]});
            var Q120;
            Q120=makeQuery(id+"F1.opExtrude","SWEPT_EDGE",EDGE,{"disambiguationData":[OSD([sQuery(id+"F0.wireOp",EDGE,"E60.MirrorCS"),sQuery(id+"F0.wireOp",EDGE,"E61.MirrorCS")])]});
            var Q121;
            Q121=makeQuery(id+"F1.opExtrude","CAP_EDGE",EDGE,{"disambiguationData":[OSD([sQuery(id+"F0.wireOp",EDGE,"E14")])],"isStart":true});
            var Q122;
            Q122=makeQuery(id+"F1.opExtrude","CAP_EDGE",EDGE,{"disambiguationData":[OSD([sQuery(id+"F0.wireOp",EDGE,"E53.MirrorCS")])],"isStart":true});
            var Q123;
            Q123=makeQuery(id+"F1.opExtrude","SWEPT_EDGE",EDGE,{"disambiguationData":[OSD([sQuery(id+"F0.wireOp",EDGE,"E16"),sQuery(id+"F0.wireOp",EDGE,"E17")])]});
            var Q124;
            Q124=makeQuery(id+"F1.opExtrude","CAP_EDGE",EDGE,{"disambiguationData":[OSD([sQuery(id+"F0.wireOp",EDGE,"5ab367f4-9cd3-4356-90f0-5b2019c22e200.MirrorCS"),sQuery(id+"F0.wireOp",EDGE,"096961d2-05df-4f17-8771-bd5e1e9e85af0.MirrorCS")])],"isStart":true});
            var Q125;
            Q125=makeQuery(id+"F1.opExtrude","SWEPT_EDGE",EDGE,{"disambiguationData":[OSD([sQuery(id+"F0.wireOp",EDGE,"E54.MirrorCS"),sQuery(id+"F0.wireOp",EDGE,"E55.MirrorCS")])]});
            var Q126;
            Q126=makeQuery(id+"F1.opExtrude","CAP_EDGE",EDGE,{"disambiguationData":[OSD([sQuery(id+"F0.wireOp",EDGE,"E58.MirrorCS")])],"isStart":true});
            var Q127;
            Q127=makeQuery(id+"F1.opExtrude","SWEPT_EDGE",EDGE,{"disambiguationData":[OSD([sQuery(id+"F0.wireOp",EDGE,"e1c94456-ab08-4bec-9781-fa68d74f9dfd0.MirrorCS"),sQuery(id+"F0.wireOp",EDGE,"E62.MirrorCS")])]});
            var Q128;
            Q128=makeQuery(id+"F1.opExtrude","SWEPT_EDGE",EDGE,{"disambiguationData":[OSD([sQuery(id+"F0.wireOp",EDGE,"E18"),sQuery(id+"F0.wireOp",EDGE,"E19")])]});
            var Q129;
            Q129=makeQuery(id+"F1.opExtrude","SWEPT_EDGE",EDGE,{"disambiguationData":[OSD([sQuery(id+"F0.wireOp",EDGE,"e1c94456-ab08-4bec-9781-fa68d74f9dfd0.MirrorCS"),sQuery(id+"F0.wireOp",EDGE,"5ab367f4-9cd3-4356-90f0-5b2019c22e200.MirrorCS")])]});
            var Q130;
            Q130=makeQuery(id+"F1.opExtrude","SWEPT_EDGE",EDGE,{"disambiguationData":[OSD([sQuery(id+"F0.wireOp",EDGE,"E17"),sQuery(id+"F0.wireOp",EDGE,"E18")])]});
            var Q131;
            Q131=makeQuery(id+"F1.opExtrude","SWEPT_EDGE",EDGE,{"disambiguationData":[OSD([sQuery(id+"F0.wireOp",EDGE,"cICnWOkE-zCsr-WVfL-8WAR-oVfGwmKeuLjA"),sQuery(id+"F0.wireOp",EDGE,"E31"),sQuery(id+"F0.wireOp",EDGE,"096961d2-05df-4f17-8771-bd5e1e9e85af0.MirrorCS")])]});
            fillet(context, id + "F2", {"entities" : qUnion([Q0, Q1, Q2, Q3, Q4, Q5, Q6, Q7, Q8, Q9, Q10, Q11, Q12, Q13, Q14, Q15, Q16, Q17, Q18, Q19, Q20, Q21, Q22, Q23, Q24, Q25, Q26, Q27, Q28, Q29, Q30, Q31, Q32, Q33, Q34, Q35, Q36, Q37, Q38, Q39, Q40, Q41, Q42, Q43, Q44, Q45, Q46, Q47, Q48, Q49, Q50, Q51, Q52, Q53, Q54, Q55, Q56, Q57, Q58, Q59, Q60, Q61, Q62, Q63, Q64, Q65, Q66, Q67, Q68, Q69, Q70, Q71, Q72, Q73, Q74, Q75, Q76, Q77, Q78, Q79, Q80, Q81, Q82, Q83, Q84, Q85, Q86, Q87, Q88, Q89, Q90, Q91, Q92, Q93, Q94, Q95, Q96, Q97, Q98, Q99, Q100, Q101, Q102, Q103, Q104, Q105, Q106, Q107, Q108, Q109, Q110, Q111, Q112, Q113, Q114, Q115, Q116, Q117, Q118, Q119, Q120, Q121, Q122, Q123, Q124, Q125, Q126, Q127, Q128, Q129, Q130, Q131]), "radius" : 1.5 * mm, "tangentPropagation" : true, "allowEdgeOverflow" : false});
        }
        {
            var Q0;
            Q0=makeQuery(id+"F1.opExtrude","CAP_FACE",FACE,{"disambiguationData":[OSD([sQuery(id+"F0.wireOp",EDGE,"E0"),sQuery(id+"F0.wireOp",EDGE,"E1"),sQuery(id+"F0.wireOp",EDGE,"E2"),sQuery(id+"F0.wireOp",EDGE,"E3"),sQuery(id+"F0.wireOp",EDGE,"E4"),sQuery(id+"F0.wireOp",EDGE,"E5"),sQuery(id+"F0.wireOp",EDGE,"E6"),sQuery(id+"F0.wireOp",EDGE,"E7"),sQuery(id+"F0.wireOp",EDGE,"E8"),sQuery(id+"F0.wireOp",EDGE,"E9"),sQuery(id+"F0.wireOp",EDGE,"E10"),sQuery(id+"F0.wireOp",EDGE,"E11"),sQuery(id+"F0.wireOp",EDGE,"E12"),sQuery(id+"F0.wireOp",EDGE,"E13"),sQuery(id+"F0.wireOp",EDGE,"E14"),sQuery(id+"F0.wireOp",EDGE,"E15"),sQuery(id+"F0.wireOp",EDGE,"E16"),sQuery(id+"F0.wireOp",EDGE,"E17"),sQuery(id+"F0.wireOp",EDGE,"E18"),sQuery(id+"F0.wireOp",EDGE,"E19"),sQuery(id+"F0.wireOp",EDGE,"E20"),sQuery(id+"F0.wireOp",EDGE,"E21"),sQuery(id+"F0.wireOp",EDGE,"E22"),sQuery(id+"F0.wireOp",EDGE,"E23"),sQuery(id+"F0.wireOp",EDGE,"E24"),sQuery(id+"F0.wireOp",EDGE,"E25"),sQuery(id+"F0.wireOp",EDGE,"E26"),sQuery(id+"F0.wireOp",EDGE,"E27"),sQuery(id+"F0.wireOp",EDGE,"E28"),sQuery(id+"F0.wireOp",EDGE,"E29"),sQuery(id+"F0.wireOp",EDGE,"E30"),sQuery(id+"F0.wireOp",EDGE,"E32.MirrorCS"),sQuery(id+"F0.wireOp",EDGE,"E33.MirrorCS"),sQuery(id+"F0.wireOp",EDGE,"E34.MirrorCS"),sQuery(id+"F0.wireOp",EDGE,"E35.MirrorCS"),sQuery(id+"F0.wireOp",EDGE,"E36.MirrorCS"),sQuery(id+"F0.wireOp",EDGE,"E37.MirrorCS"),sQuery(id+"F0.wireOp",EDGE,"E38.MirrorCS"),sQuery(id+"F0.wireOp",EDGE,"E39.MirrorCS"),sQuery(id+"F0.wireOp",EDGE,"E40.MirrorCS"),sQuery(id+"F0.wireOp",EDGE,"E41.MirrorCS"),sQuery(id+"F0.wireOp",EDGE,"E42.MirrorCS"),sQuery(id+"F0.wireOp",EDGE,"E43.MirrorCS"),sQuery(id+"F0.wireOp",EDGE,"E44.MirrorCS"),sQuery(id+"F0.wireOp",EDGE,"E45.MirrorCS"),sQuery(id+"F0.wireOp",EDGE,"E46.MirrorCS"),sQuery(id+"F0.wireOp",EDGE,"E47.MirrorCS"),sQuery(id+"F0.wireOp",EDGE,"E48.MirrorCS"),sQuery(id+"F0.wireOp",EDGE,"E49.MirrorCS"),sQuery(id+"F0.wireOp",EDGE,"E50.MirrorCS"),sQuery(id+"F0.wireOp",EDGE,"E51.MirrorCS"),sQuery(id+"F0.wireOp",EDGE,"E52.MirrorCS"),sQuery(id+"F0.wireOp",EDGE,"E54.MirrorCS"),sQuery(id+"F0.wireOp",EDGE,"E53.MirrorCS"),sQuery(id+"F0.wireOp",EDGE,"E55.MirrorCS"),sQuery(id+"F0.wireOp",EDGE,"E56.MirrorCS"),sQuery(id+"F0.wireOp",EDGE,"E57.MirrorCS"),sQuery(id+"F0.wireOp",EDGE,"E58.MirrorCS"),sQuery(id+"F0.wireOp",EDGE,"E59.MirrorCS"),sQuery(id+"F0.wireOp",EDGE,"E60.MirrorCS"),sQuery(id+"F0.wireOp",EDGE,"E61.MirrorCS"),sQuery(id+"F0.wireOp",EDGE,"E62.MirrorCS"),sQuery(id+"F0.wireOp",EDGE,"E63"),sQuery(id+"F0.wireOp",EDGE,"E64")])],"isStart":false});
            var sketch = newSketch(context, id + "F3", { "sketchPlane" : qUnion([Q0])});
            skText(sketch, "E65", { "text": "Nala", "fontName": "OpenSans-Regular.ttf"});
            const initialGuessF3  = {"E65": [-0.0282, -0.00742, 1, 0, 0.01347]};
            skSetInitialGuess(sketch, initialGuessF3);
            skSolve(sketch);
        }
        {
            var Q0;
            Q0 = qSketchRegion(id + "F3", true);
            extrude(context, id + "F4", {"entities" : qUnion([Q0]), "operationType" : NewBodyOperationType.ADD, "depth" : 1 * mm, "offsetDistance" : 25 * mm});
        }
        {
            var Q0;
            Q0=makeQuery(id+"F1.opExtrude","CAP_FACE",FACE,{"disambiguationData":[OSD([sQuery(id+"F0.wireOp",EDGE,"E0"),sQuery(id+"F0.wireOp",EDGE,"E1"),sQuery(id+"F0.wireOp",EDGE,"E2"),sQuery(id+"F0.wireOp",EDGE,"E3"),sQuery(id+"F0.wireOp",EDGE,"E4"),sQuery(id+"F0.wireOp",EDGE,"E5"),sQuery(id+"F0.wireOp",EDGE,"E6"),sQuery(id+"F0.wireOp",EDGE,"E7"),sQuery(id+"F0.wireOp",EDGE,"E8"),sQuery(id+"F0.wireOp",EDGE,"E9"),sQuery(id+"F0.wireOp",EDGE,"E10"),sQuery(id+"F0.wireOp",EDGE,"E11"),sQuery(id+"F0.wireOp",EDGE,"E12"),sQuery(id+"F0.wireOp",EDGE,"E13"),sQuery(id+"F0.wireOp",EDGE,"E14"),sQuery(id+"F0.wireOp",EDGE,"E15"),sQuery(id+"F0.wireOp",EDGE,"E16"),sQuery(id+"F0.wireOp",EDGE,"E17"),sQuery(id+"F0.wireOp",EDGE,"E18"),sQuery(id+"F0.wireOp",EDGE,"E19"),sQuery(id+"F0.wireOp",EDGE,"E20"),sQuery(id+"F0.wireOp",EDGE,"E21"),sQuery(id+"F0.wireOp",EDGE,"E22"),sQuery(id+"F0.wireOp",EDGE,"E23"),sQuery(id+"F0.wireOp",EDGE,"E24"),sQuery(id+"F0.wireOp",EDGE,"E25"),sQuery(id+"F0.wireOp",EDGE,"E26"),sQuery(id+"F0.wireOp",EDGE,"E27"),sQuery(id+"F0.wireOp",EDGE,"E28"),sQuery(id+"F0.wireOp",EDGE,"E29"),sQuery(id+"F0.wireOp",EDGE,"E30"),sQuery(id+"F0.wireOp",EDGE,"E32.MirrorCS"),sQuery(id+"F0.wireOp",EDGE,"E33.MirrorCS"),sQuery(id+"F0.wireOp",EDGE,"E34.MirrorCS"),sQuery(id+"F0.wireOp",EDGE,"E35.MirrorCS"),sQuery(id+"F0.wireOp",EDGE,"E36.MirrorCS"),sQuery(id+"F0.wireOp",EDGE,"E37.MirrorCS"),sQuery(id+"F0.wireOp",EDGE,"E38.MirrorCS"),sQuery(id+"F0.wireOp",EDGE,"E39.MirrorCS"),sQuery(id+"F0.wireOp",EDGE,"E40.MirrorCS"),sQuery(id+"F0.wireOp",EDGE,"E41.MirrorCS"),sQuery(id+"F0.wireOp",EDGE,"E42.MirrorCS"),sQuery(id+"F0.wireOp",EDGE,"E43.MirrorCS"),sQuery(id+"F0.wireOp",EDGE,"E44.MirrorCS"),sQuery(id+"F0.wireOp",EDGE,"E45.MirrorCS"),sQuery(id+"F0.wireOp",EDGE,"E46.MirrorCS"),sQuery(id+"F0.wireOp",EDGE,"E47.MirrorCS"),sQuery(id+"F0.wireOp",EDGE,"E48.MirrorCS"),sQuery(id+"F0.wireOp",EDGE,"E49.MirrorCS"),sQuery(id+"F0.wireOp",EDGE,"E50.MirrorCS"),sQuery(id+"F0.wireOp",EDGE,"E51.MirrorCS"),sQuery(id+"F0.wireOp",EDGE,"E52.MirrorCS"),sQuery(id+"F0.wireOp",EDGE,"E54.MirrorCS"),sQuery(id+"F0.wireOp",EDGE,"E53.MirrorCS"),sQuery(id+"F0.wireOp",EDGE,"E55.MirrorCS"),sQuery(id+"F0.wireOp",EDGE,"E56.MirrorCS"),sQuery(id+"F0.wireOp",EDGE,"E57.MirrorCS"),sQuery(id+"F0.wireOp",EDGE,"E58.MirrorCS"),sQuery(id+"F0.wireOp",EDGE,"E59.MirrorCS"),sQuery(id+"F0.wireOp",EDGE,"E60.MirrorCS"),sQuery(id+"F0.wireOp",EDGE,"E61.MirrorCS"),sQuery(id+"F0.wireOp",EDGE,"E62.MirrorCS"),sQuery(id+"F0.wireOp",EDGE,"E63"),sQuery(id+"F0.wireOp",EDGE,"E64")])],"isStart":true});
            var sketch = newSketch(context, id + "F5", { "sketchPlane" : qUnion([Q0])});
            skText(sketch, "E66", { "text": "I\'m Lost, Please Call\n    (707)-465-1095", "fontName": "OpenSans-Regular.ttf"});
            const initialGuessF5  = {"E66": [-0.03087, 0.0036, 1, 0, 0.00332]};
            skSetInitialGuess(sketch, initialGuessF5);
            skSolve(sketch);
        }
        {
            var Q0;
            Q0 = qSketchRegion(id + "F5", true);
            extrude(context, id + "F6", {"entities" : qUnion([Q0]), "operationType" : NewBodyOperationType.ADD, "oppositeDirection" : true, "depth" : 1 * mm, "offsetDistance" : 25 * mm});
        }
        {
            var Q0;
            Q0=makeQuery(id+"F1.opExtrude","CAP_EDGE",EDGE,{"disambiguationData":[OSD([sQuery(id+"F0.wireOp",EDGE,"E63")])],"isStart":false});
            var Q1;
            Q1=makeQuery(id+"F1.opExtrude","CAP_EDGE",EDGE,{"disambiguationData":[OSD([sQuery(id+"F0.wireOp",EDGE,"E63")])],"isStart":true});
            fillet(context, id + "F7", {"entities" : qUnion([Q0, Q1]), "radius" : .5 * mm, "tangentPropagation" : true, "allowEdgeOverflow" : false});
        }
    });
